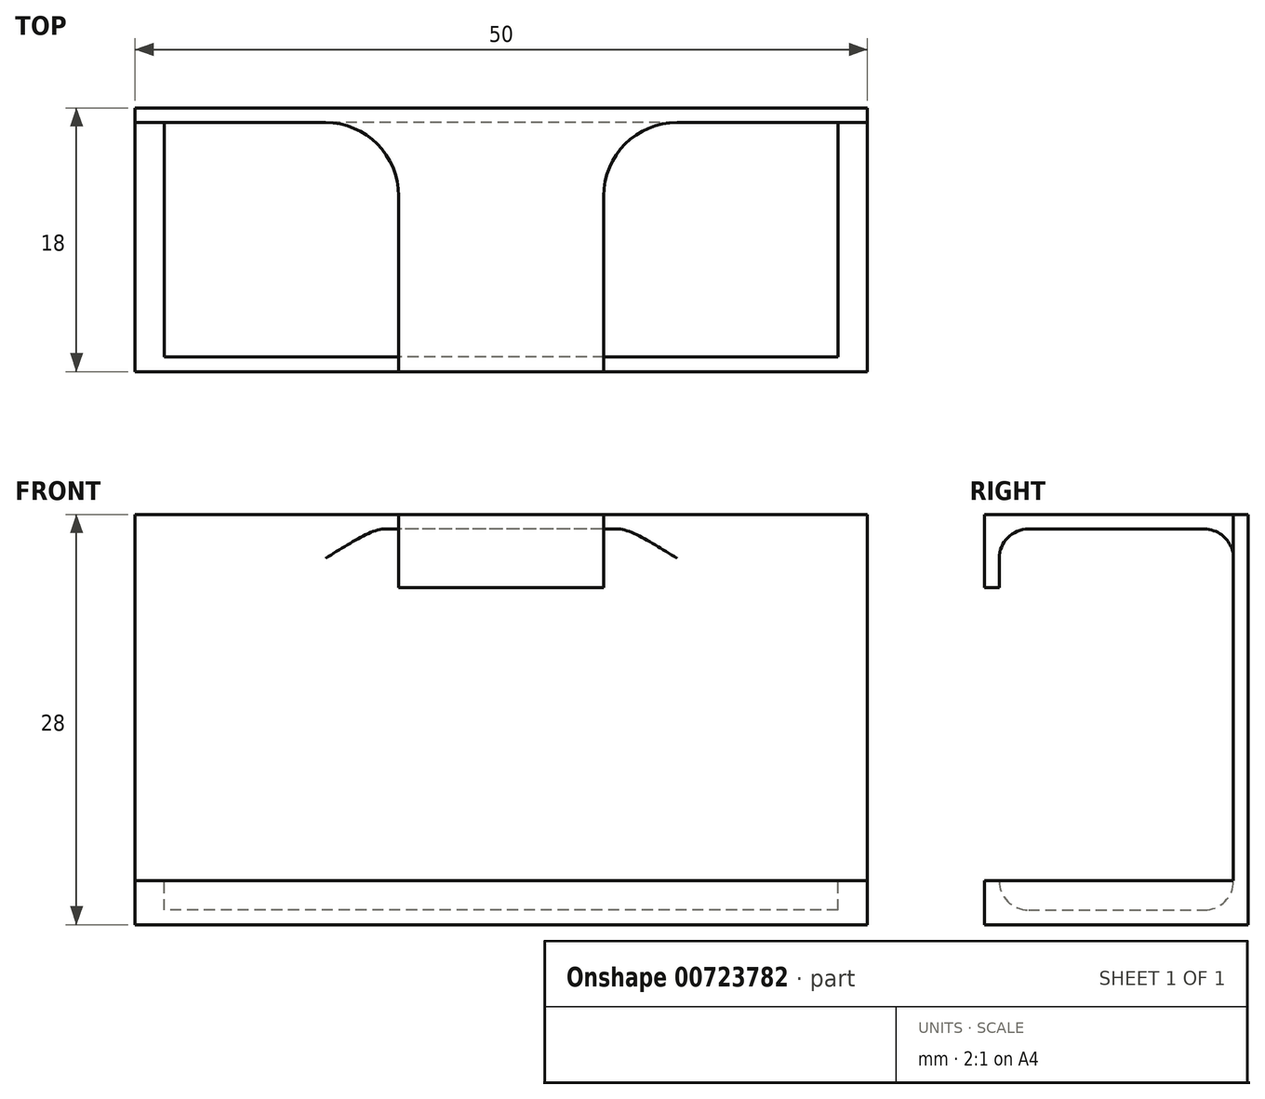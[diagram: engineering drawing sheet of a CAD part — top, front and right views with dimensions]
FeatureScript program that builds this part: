
annotation { "Feature Type Name" : "Feature", "Feature Type Description" : "" }
export const myFeature = defineFeature(function(context is Context, id is Id, definition is map)
    precondition{}
    {
        {
            var Q0;
            Q0=qCreatedBy(makeId("Right.planeOp"),FACE);
            var sketch = newSketch(context, id + "F0", { "sketchPlane" : qUnion([Q0])});
            skLineSegment(sketch, "E0", {"start": v(0, 0) * mm, "end": v(-16, 0) * mm});
            skLineSegment(sketch, "E1", {"start": v(0, 0) * mm, "end": v(0, 26) * mm});
            skLineSegment(sketch, "E2", {"start": v(0, 26) * mm, "end": v(1, 26) * mm});
            skLineSegment(sketch, "E3", {"start": v(1, 26) * mm, "end": v(1, -1) * mm});
            skLineSegment(sketch, "E4", {"start": v(-16, 0) * mm, "end": v(-16, 2) * mm});
            skLineSegment(sketch, "E5", {"start": v(-17, 2) * mm, "end": v(-17, -1) * mm});
            skLineSegment(sketch, "E6", {"start": v(-16, 2) * mm, "end": v(-17, 2) * mm});
            skLineSegment(sketch, "E7", {"start": v(1, -1) * mm, "end": v(-17, -1) * mm});
            skLineSegment(sketch, "E8", {"start": v(0, 26) * mm, "end": v(-16, 26) * mm});
            skLineSegment(sketch, "E9", {"start": v(-16, 26) * mm, "end": v(-16, 22) * mm});
            skLineSegment(sketch, "E10", {"start": v(-16, 22) * mm, "end": v(-17, 22) * mm});
            skLineSegment(sketch, "E11", {"start": v(-17, 22) * mm, "end": v(-17, 27) * mm});
            skLineSegment(sketch, "E12", {"start": v(-17, 27) * mm, "end": v(1, 27) * mm});
            skLineSegment(sketch, "E13", {"start": v(1, 27) * mm, "end": v(1, 26) * mm});
            skSolve(sketch);
        }
        {
            var Q0;
            Q0=makeQuery(id+"F0.imprint","IMPRINT",FACE,{"disambiguationData":[TD([[makeQuery(id+"F0.imprint","IMPRINT",EDGE,{"derivedFrom":sQuery(id+"F0.wireOp",EDGE,"E0")}),1.0]])]});
            var Q1;
            Q1=makeQuery(id+"F0.imprint","IMPRINT",FACE,{"disambiguationData":[TD([[makeQuery(id+"F0.imprint","IMPRINT",EDGE,{"derivedFrom":sQuery(id+"F0.wireOp",EDGE,"E2")}),1.0]])]});
            extrude(context, id + "F1", {"entities" : qUnion([Q0, Q1]), "depth" : 50 * mm, "offsetDistance" : 25 * mm});
        }
        {
            var Q0;
            Q0=makeQuery(id+"F1.opExtrude","SWEPT_FACE",FACE,{"disambiguationData":[OSD([sQuery(id+"F0.wireOp",EDGE,"E0")])]});
            var sketch = newSketch(context, id + "F2", { "sketchPlane" : qUnion([Q0])});
            skLineSegment(sketch, "E14.bottom", {"start": v(50, -16) * mm, "end": v(48, -16) * mm});
            skLineSegment(sketch, "E14.top", {"start": v(50, 0) * mm, "end": v(48, 0) * mm});
            skLineSegment(sketch, "E14.left", {"start": v(50, -16) * mm, "end": v(50, 0) * mm});
            skLineSegment(sketch, "E14.right", {"start": v(48, -16) * mm, "end": v(48, 0) * mm});
            skLineSegment(sketch, "E15.bottom", {"start": v(0, -16) * mm, "end": v(2, -16) * mm});
            skLineSegment(sketch, "E15.top", {"start": v(0, 0) * mm, "end": v(2, 0) * mm});
            skLineSegment(sketch, "E15.left", {"start": v(0, -16) * mm, "end": v(0, 0) * mm});
            skLineSegment(sketch, "E15.right", {"start": v(2, -16) * mm, "end": v(2, 0) * mm});
            skSolve(sketch);
        }
        {
            var Q0;
            Q0=makeQuery(id+"F2.imprint","IMPRINT",FACE,{"disambiguationData":[TD([[makeQuery(id+"F2.imprint","IMPRINT",EDGE,{"derivedFrom":sQuery(id+"F2.wireOp",EDGE,"E15.bottom")}),-1.0]])]});
            var Q1;
            Q1=makeQuery(id+"F2.imprint","IMPRINT",FACE,{"disambiguationData":[TD([[makeQuery(id+"F2.imprint","IMPRINT",EDGE,{"derivedFrom":sQuery(id+"F2.wireOp",EDGE,"E14.bottom")}),-1.0]])]});
            extrude(context, id + "F3", {"entities" : qUnion([Q0, Q1]), "operationType" : NewBodyOperationType.ADD, "depth" : 2 * mm, "offsetDistance" : 25 * mm});
        }
        {
            var Q0;
            Q0=makeQuery(id+"F1.opExtrude","SWEPT_FACE",FACE,{"disambiguationData":[OSD([sQuery(id+"F0.wireOp",EDGE,"E12")])]});
            var sketch = newSketch(context, id + "F4", { "sketchPlane" : qUnion([Q0])});
            skLineSegment(sketch, "E16.bottom", {"start": v(50, 0) * mm, "end": v(32, 0) * mm});
            skLineSegment(sketch, "E16.top", {"start": v(50, -17) * mm, "end": v(32, -17) * mm});
            skLineSegment(sketch, "E16.left", {"start": v(50, 0) * mm, "end": v(50, -17) * mm});
            skLineSegment(sketch, "E16.right", {"start": v(32, 0) * mm, "end": v(32, -17) * mm});
            skLineSegment(sketch, "E17.bottom", {"start": v(0, 0) * mm, "end": v(18, 0) * mm});
            skLineSegment(sketch, "E17.top", {"start": v(0, -17) * mm, "end": v(18, -17) * mm});
            skLineSegment(sketch, "E17.left", {"start": v(0, 0) * mm, "end": v(0, -17) * mm});
            skLineSegment(sketch, "E17.right", {"start": v(18, 0) * mm, "end": v(18, -17) * mm});
            skSolve(sketch);
        }
        {
            var Q0;
            Q0=makeQuery(id+"F4.imprint","IMPRINT",FACE,{"disambiguationData":[TD([[makeQuery(id+"F4.imprint","IMPRINT",EDGE,{"derivedFrom":sQuery(id+"F4.wireOp",EDGE,"E17.bottom")}),-1.0]])]});
            var Q1;
            Q1=makeQuery(id+"F4.imprint","IMPRINT",FACE,{"disambiguationData":[TD([[makeQuery(id+"F4.imprint","IMPRINT",EDGE,{"derivedFrom":sQuery(id+"F4.wireOp",EDGE,"E16.bottom")}),1.0]])]});
            extrude(context, id + "F5", {"entities" : qUnion([Q0, Q1]), "operationType" : NewBodyOperationType.REMOVE, "oppositeDirection" : true, "depth" : 25 * mm, "offsetDistance" : 25 * mm});
        }
        {
            var Q0;
            Q0=makeQuery(id+"F1.opExtrude","SWEPT_EDGE",EDGE,{"disambiguationData":[OSD([sQuery(id+"F0.wireOp",EDGE,"E1"),sQuery(id+"F0.wireOp",EDGE,"E2"),sQuery(id+"F0.wireOp",EDGE,"E8")])]});
            var Q1;
            Q1=makeQuery(id+"F1.opExtrude","SWEPT_EDGE",EDGE,{"disambiguationData":[OSD([sQuery(id+"F0.wireOp",EDGE,"E8"),sQuery(id+"F0.wireOp",EDGE,"E9")])]});
            var Q2;
            Q2=makeQuery(id+"F1.opExtrude","SWEPT_EDGE",EDGE,{"disambiguationData":[OSD([sQuery(id+"F0.wireOp",EDGE,"E0"),sQuery(id+"F0.wireOp",EDGE,"E1")])]});
            var Q3;
            Q3=makeQuery(id+"F3.opExtrude","CAP_EDGE",EDGE,{"disambiguationData":[OSD([sQuery(id+"F2.wireOp",EDGE,"E14.top")])],"isStart":false});
            var Q4;
            Q4=makeQuery(id+"F3.opExtrude","CAP_EDGE",EDGE,{"disambiguationData":[OSD([sQuery(id+"F2.wireOp",EDGE,"E15.top")])],"isStart":false});
            fillet(context, id + "F6", {"entities" : qUnion([Q0, Q1, Q2, Q3, Q4]), "radius" : 2 * mm, "tangentPropagation" : true, "allowEdgeOverflow" : false});
        }
        {
            var Q0;
            Q0=makeQuery(id+"F5.boolean.opBoolean","COPY",EDGE,{"derivedFrom":makeQuery(id+"F5.opExtrude","SWEPT_EDGE",EDGE,{"disambiguationData":[OSD([sQuery(id+"F4.wireOp",EDGE,"E16.bottom"),sQuery(id+"F4.wireOp",EDGE,"E16.right")])]})});
            var Q1;
            Q1=makeQuery(id+"F5.boolean.opBoolean","COPY",EDGE,{"derivedFrom":makeQuery(id+"F5.opExtrude","SWEPT_EDGE",EDGE,{"disambiguationData":[OSD([sQuery(id+"F4.wireOp",EDGE,"E17.bottom"),sQuery(id+"F4.wireOp",EDGE,"E17.right")])]})});
            fillet(context, id + "F7", {"entities" : qUnion([Q0, Q1]), "radius" : 5 * mm, "tangentPropagation" : true, "allowEdgeOverflow" : false});
        }
        {
            var Q0;
            Q0=makeQuery(id+"F1.opExtrude","SWEPT_EDGE",EDGE,{"disambiguationData":[OSD([sQuery(id+"F0.wireOp",EDGE,"E0"),sQuery(id+"F0.wireOp",EDGE,"E4")])]});
            fillet(context, id + "F8", {"entities" : qUnion([Q0]), "radius" : 2 * mm, "tangentPropagation" : true, "allowEdgeOverflow" : false});
        }
    });
